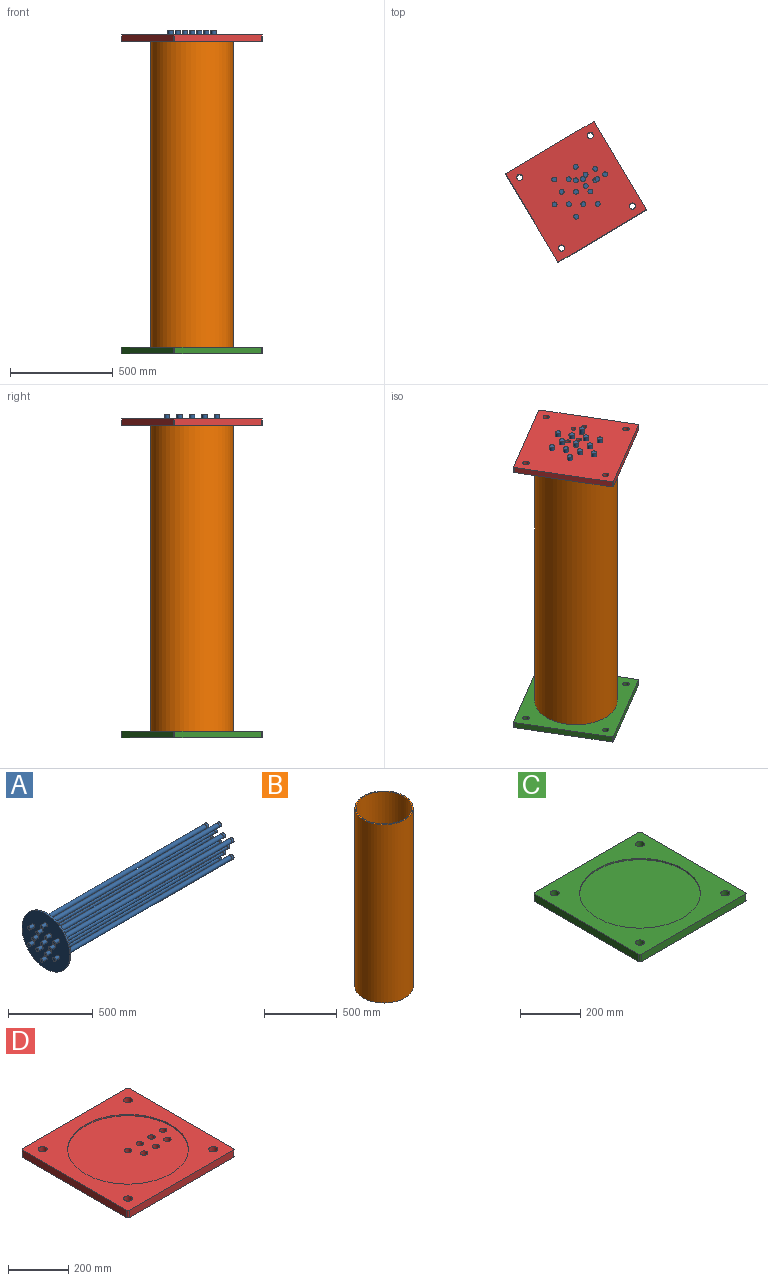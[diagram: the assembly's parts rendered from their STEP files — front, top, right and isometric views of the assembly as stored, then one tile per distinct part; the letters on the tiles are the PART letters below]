
ASSEMBLY  parts=4 mates=6
PART A: 133 faces, bbox 1490x400x400 mm
  f0: plane 31.5x31.5mm, normal (1,0,0), area 779.3mm2, adj f1
  f1: cylinder r=15.75mm len=31.5mm, axis (-1,0,0), area 1682.3mm2, adj f0,f2
  f2: plane 31.5x31.5mm, normal (-1,0,0), area 72.5mm2, adj f1,f3
  f3: cylinder r=15mm len=1394mm, axis (-1,0,0), area 131381.4mm2, adj f2,f4
  f4: plane 31.5x31.5mm, normal (1,0,0), area 72.5mm2, adj f3,f5
  f5: cylinder r=15.75mm len=31.5mm, axis (-1,0,0), area 2375mm2, adj f4,f6
  f6: plane 40x40mm, normal (1,0,0), area 477.3mm2, adj f5,f7
  f7: cylinder r=20mm len=40mm, axis (-1,0,0), area 1005.3mm2, adj f6,f106
  f8: plane 31.5x31.5mm, normal (1,0,0), area 779.3mm2, adj f9
  f9: cylinder r=15.75mm len=31.5mm, axis (-1,0,0), area 1682.3mm2, adj f8,f10
  f10: plane 31.5x31.5mm, normal (-1,0,0), area 72.5mm2, adj f9,f11
  f11: cylinder r=15mm len=1394mm, axis (-1,0,0), area 131381.4mm2, adj f10,f12
  f12: plane 31.5x31.5mm, normal (1,0,0), area 72.5mm2, adj f11,f13
  f13: cylinder r=15.75mm len=31.5mm, axis (-1,0,0), area 2375mm2, adj f12,f14
  f14: plane 40x40mm, normal (1,0,0), area 477.3mm2, adj f13,f15
  f15: cylinder r=20mm len=40mm, axis (-1,0,0), area 1005.3mm2, adj f14,f106
  f16: plane 31.5x31.5mm, normal (1,0,0), area 779.3mm2, adj f17
  f17: cylinder r=15.75mm len=31.5mm, axis (-1,0,0), area 1682.3mm2, adj f16,f18
  f18: plane 31.5x31.5mm, normal (-1,0,0), area 72.5mm2, adj f17,f19
  f19: cylinder r=15mm len=1394mm, axis (-1,0,0), area 131381.4mm2, adj f18,f20
  f20: plane 31.5x31.5mm, normal (1,0,0), area 72.5mm2, adj f19,f21
  f21: cylinder r=15.75mm len=31.5mm, axis (-1,0,0), area 2375mm2, adj f20,f22
  f22: plane 40x40mm, normal (1,0,0), area 477.3mm2, adj f21,f23
  f23: cylinder r=20mm len=40mm, axis (-1,0,0), area 1005.3mm2, adj f22,f106
  f24: plane 31.5x31.5mm, normal (1,0,0), area 779.3mm2, adj f25
  f25: cylinder r=15.75mm len=31.5mm, axis (-1,0,0), area 1682.3mm2, adj f24,f26
  f26: plane 31.5x31.5mm, normal (-1,0,0), area 72.5mm2, adj f25,f27
  f27: cylinder r=15mm len=1394mm, axis (-1,0,0), area 131381.4mm2, adj f26,f28
  f28: plane 31.5x31.5mm, normal (1,0,0), area 72.5mm2, adj f27,f29
  f29: cylinder r=15.75mm len=31.5mm, axis (-1,0,0), area 2375mm2, adj f28,f30
  f30: plane 40x40mm, normal (1,0,0), area 477.3mm2, adj f29,f31
  f31: cylinder r=20mm len=40mm, axis (-1,0,0), area 1005.3mm2, adj f30,f106
  f32: plane 31.5x31.5mm, normal (1,0,0), area 779.3mm2, adj f33
  f33: cylinder r=15.75mm len=31.5mm, axis (-1,0,0), area 1682.3mm2, adj f32,f34
  f34: plane 31.5x31.5mm, normal (-1,0,0), area 72.5mm2, adj f33,f35
  f35: cylinder r=15mm len=1394mm, axis (-1,0,0), area 131381.4mm2, adj f34,f36
  f36: plane 31.5x31.5mm, normal (1,0,0), area 72.5mm2, adj f35,f37
  f37: cylinder r=15.75mm len=31.5mm, axis (-1,0,0), area 2375mm2, adj f36,f38
  f38: plane 40x40mm, normal (1,0,0), area 477.3mm2, adj f37,f39
  f39: cylinder r=20mm len=40mm, axis (-1,0,0), area 1005.3mm2, adj f38,f106
  f40: plane 31.5x31.5mm, normal (1,0,0), area 779.3mm2, adj f41
  f41: cylinder r=15.75mm len=31.5mm, axis (-1,0,0), area 1682.3mm2, adj f40,f42
  f42: plane 31.5x31.5mm, normal (-1,0,0), area 72.5mm2, adj f41,f43
  f43: cylinder r=15mm len=1394mm, axis (-1,0,0), area 131381.4mm2, adj f42,f44
  f44: plane 31.5x31.5mm, normal (1,0,0), area 72.5mm2, adj f43,f45
  f45: cylinder r=15.75mm len=31.5mm, axis (-1,0,0), area 2375mm2, adj f44,f46
  f46: plane 40x40mm, normal (1,0,0), area 477.3mm2, adj f45,f47
  f47: cylinder r=20mm len=40mm, axis (-1,0,0), area 1005.3mm2, adj f46,f106
  f48: plane 31.5x31.5mm, normal (1,0,0), area 779.3mm2, adj f49
  f49: cylinder r=15.75mm len=31.5mm, axis (-1,0,0), area 1682.3mm2, adj f48,f50
  f50: plane 31.5x31.5mm, normal (-1,0,0), area 72.5mm2, adj f49,f51
  f51: cylinder r=15mm len=1394mm, axis (-1,0,0), area 131381.4mm2, adj f50,f52
  f52: plane 31.5x31.5mm, normal (1,0,0), area 72.5mm2, adj f51,f53
  f53: cylinder r=15.75mm len=31.5mm, axis (-1,0,0), area 2375mm2, adj f52,f54
  f54: plane 40x40mm, normal (1,0,0), area 477.3mm2, adj f53,f55
  f55: cylinder r=20mm len=40mm, axis (-1,0,0), area 1005.3mm2, adj f54,f106
  f56: plane 31.5x31.5mm, normal (1,0,0), area 779.3mm2, adj f57
  f57: cylinder r=15.75mm len=31.5mm, axis (-1,0,0), area 1682.3mm2, adj f56,f58
  f58: plane 31.5x31.5mm, normal (-1,0,0), area 72.5mm2, adj f57,f59
  f59: cylinder r=15mm len=1394mm, axis (-1,0,0), area 131381.4mm2, adj f58,f60
  f60: plane 31.5x31.5mm, normal (1,0,0), area 72.5mm2, adj f59,f61
  f61: cylinder r=15.75mm len=31.5mm, axis (-1,0,0), area 2375mm2, adj f60,f62
  f62: plane 40x40mm, normal (1,0,0), area 477.3mm2, adj f61,f63
  f63: cylinder r=20mm len=40mm, axis (-1,0,0), area 1005.3mm2, adj f62,f106
  f64: plane 31.5x31.5mm, normal (1,0,0), area 779.3mm2, adj f65
  f65: cylinder r=15.75mm len=31.5mm, axis (-1,0,0), area 1682.3mm2, adj f64,f66
  f66: plane 31.5x31.5mm, normal (-1,0,0), area 72.5mm2, adj f65,f67
  f67: cylinder r=15mm len=1394mm, axis (-1,0,0), area 131381.4mm2, adj f66,f68
  f68: plane 31.5x31.5mm, normal (1,0,0), area 72.5mm2, adj f67,f69
  f69: cylinder r=15.75mm len=31.5mm, axis (-1,0,0), area 2375mm2, adj f68,f70
  f70: plane 40x40mm, normal (1,0,0), area 477.3mm2, adj f69,f71
  f71: cylinder r=20mm len=40mm, axis (-1,0,0), area 1005.3mm2, adj f70,f106
  f72: plane 31.5x31.5mm, normal (1,0,0), area 779.3mm2, adj f73
  f73: cylinder r=15.75mm len=31.5mm, axis (-1,0,0), area 1682.3mm2, adj f72,f74
  f74: plane 31.5x31.5mm, normal (-1,0,0), area 72.5mm2, adj f73,f75
  f75: cylinder r=15mm len=1394mm, axis (-1,0,0), area 131381.4mm2, adj f74,f76
  f76: plane 31.5x31.5mm, normal (1,0,0), area 72.5mm2, adj f75,f77
  f77: cylinder r=15.75mm len=31.5mm, axis (-1,0,0), area 2375mm2, adj f76,f78
  f78: plane 40x40mm, normal (1,0,0), area 477.3mm2, adj f77,f79
  f79: cylinder r=20mm len=40mm, axis (-1,0,0), area 1005.3mm2, adj f78,f106
  f80: plane 31.5x31.5mm, normal (1,0,0), area 779.3mm2, adj f81
  f81: cylinder r=15.75mm len=31.5mm, axis (-1,0,0), area 1682.3mm2, adj f80,f82
  f82: plane 31.5x31.5mm, normal (-1,0,0), area 72.5mm2, adj f81,f83
  f83: cylinder r=15mm len=1394mm, axis (-1,0,0), area 131381.4mm2, adj f82,f84
  f84: plane 31.5x31.5mm, normal (1,0,0), area 72.5mm2, adj f83,f85
  f85: cylinder r=15.75mm len=31.5mm, axis (-1,0,0), area 2375mm2, adj f84,f86
  f86: plane 40x40mm, normal (1,0,0), area 477.3mm2, adj f85,f87
  f87: cylinder r=20mm len=40mm, axis (-1,0,0), area 1005.3mm2, adj f86,f106
  f88: plane 31.5x31.5mm, normal (1,0,0), area 779.3mm2, adj f89
  f89: cylinder r=15.75mm len=31.5mm, axis (-1,0,0), area 1682.3mm2, adj f88,f90
  f90: plane 31.5x31.5mm, normal (-1,0,0), area 72.5mm2, adj f89,f91
  f91: cylinder r=15mm len=1394mm, axis (-1,0,0), area 131381.4mm2, adj f90,f92
  f92: plane 31.5x31.5mm, normal (1,0,0), area 72.5mm2, adj f91,f93
  f93: cylinder r=15.75mm len=31.5mm, axis (-1,0,0), area 2375mm2, adj f92,f94
  f94: plane 40x40mm, normal (1,0,0), area 477.3mm2, adj f93,f95
  f95: cylinder r=20mm len=40mm, axis (-1,0,0), area 1005.3mm2, adj f94,f106
  f96: plane 31.5x31.5mm, normal (1,0,0), area 779.3mm2, adj f97
  f97: cylinder r=15.75mm len=31.5mm, axis (-1,0,0), area 1682.3mm2, adj f96,f98
  f98: plane 31.5x31.5mm, normal (-1,0,0), area 72.5mm2, adj f97,f99
  f99: cylinder r=15mm len=1394mm, axis (-1,0,0), area 131381.4mm2, adj f98,f100
  f100: plane 31.5x31.5mm, normal (1,0,0), area 72.5mm2, adj f99,f101
  f101: cylinder r=15.75mm len=31.5mm, axis (-1,0,0), area 2375mm2, adj f100,f102
  f102: plane 40x40mm, normal (1,0,0), area 477.3mm2, adj f101,f103
  f103: cylinder r=20mm len=40mm, axis (-1,0,0), area 1005.3mm2, adj f102,f106
  f104: cylinder r=200mm len=400mm, axis (1,0,0), area 12566.4mm2, adj f105,f106
  f105: plane 400x400mm, normal (-1,0,0), area 119880.3mm2, adj f104,f108,f110,f112,f114,f116,f118,f120
  f106: plane 400x400mm, normal (1,0,0), area 109327.4mm2, adj f7,f15,f23,f31,f39,f47,f55,f63
  f107: plane 23.8x23.8mm, normal (-1,0,0), area 444.9mm2, adj f108
  f108: cylinder r=11.9mm len=37mm, axis (-1,0,0), area 2766.5mm2, adj f105,f107
  f109: plane 23.8x23.8mm, normal (-1,0,0), area 444.9mm2, adj f110
  f110: cylinder r=11.9mm len=37mm, axis (-1,0,0), area 2766.5mm2, adj f105,f109
  f111: plane 23.8x23.8mm, normal (-1,0,0), area 444.9mm2, adj f112
  f112: cylinder r=11.9mm len=37mm, axis (-1,0,0), area 2766.5mm2, adj f105,f111
  f113: plane 23.8x23.8mm, normal (-1,0,0), area 444.9mm2, adj f114
  f114: cylinder r=11.9mm len=37mm, axis (-1,0,0), area 2766.5mm2, adj f105,f113
  f115: plane 23.8x23.8mm, normal (-1,0,0), area 444.9mm2, adj f116
  f116: cylinder r=11.9mm len=37mm, axis (-1,0,0), area 2766.5mm2, adj f105,f115
  f117: plane 23.8x23.8mm, normal (-1,0,0), area 444.9mm2, adj f118
  f118: cylinder r=11.9mm len=37mm, axis (-1,0,0), area 2766.5mm2, adj f105,f117
  f119: plane 23.8x23.8mm, normal (-1,0,0), area 444.9mm2, adj f120
  f120: cylinder r=11.9mm len=37mm, axis (-1,0,0), area 2766.5mm2, adj f105,f119
  f121: plane 23.8x23.8mm, normal (-1,0,0), area 444.9mm2, adj f122
  f122: cylinder r=11.9mm len=37mm, axis (-1,0,0), area 2766.5mm2, adj f105,f121
  f123: plane 23.8x23.8mm, normal (-1,0,0), area 444.9mm2, adj f124
  f124: cylinder r=11.9mm len=37mm, axis (-1,0,0), area 2766.5mm2, adj f105,f123
  f125: plane 23.8x23.8mm, normal (-1,0,0), area 444.9mm2, adj f126
  f126: cylinder r=11.9mm len=37mm, axis (-1,0,0), area 2766.5mm2, adj f105,f125
  f127: plane 23.8x23.8mm, normal (-1,0,0), area 444.9mm2, adj f128
  f128: cylinder r=11.9mm len=37mm, axis (-1,0,0), area 2766.5mm2, adj f105,f127
  f129: plane 23.8x23.8mm, normal (-1,0,0), area 444.9mm2, adj f130
  f130: cylinder r=11.9mm len=37mm, axis (-1,0,0), area 2766.5mm2, adj f105,f129
  f131: plane 23.8x23.8mm, normal (-1,0,0), area 444.9mm2, adj f132
  f132: cylinder r=11.9mm len=37mm, axis (-1,0,0), area 2766.5mm2, adj f105,f131
PART B: 4 faces, bbox 400x400x1500 mm
  f0: cylinder r=192mm len=1500mm, axis (0,0,-1), area 1809557.4mm2, adj f2,f3
  f1: cylinder r=200mm len=1500mm, axis (0,0,-1), area 1884955.6mm2, adj f2,f3
  f2: plane 400x400mm, normal (0,0,1), area 9852mm2, adj f0,f1
  f3: plane 400x400mm, normal (0,0,-1), area 9852mm2, adj f0,f1
PART C: 16 faces, bbox 500x500x30 mm
  f0: plane 490x30mm, normal (1,0,0), area 14700mm2, adj f8,f9,f10,f13
  f1: plane 490x30mm, normal (0,1,0), area 14700mm2, adj f8,f9,f10,f11
  f2: plane 490x30mm, normal (-1,0,0), area 14700mm2, adj f8,f9,f11,f12
  f3: cylinder r=15mm len=30mm, axis (0,0,-1), area 2827.4mm2, adj f8,f9
  f4: plane 490x30mm, normal (0,-1,0), area 14700mm2, adj f8,f9,f12,f13
  f5: cylinder r=15mm len=30mm, axis (0,0,-1), area 2827.4mm2, adj f8,f9
  f6: cylinder r=15mm len=30mm, axis (0,0,-1), area 2827.4mm2, adj f8,f9
  f7: cylinder r=15mm len=30mm, axis (0,0,-1), area 2827.4mm2, adj f8,f9
  f8: plane 500x500mm, normal (0,0,1), area 121487.4mm2, adj f0,f1,f2,f3,f4,f5,f6,f7
  f9: plane 500x500mm, normal (0,0,-1), area 247151.1mm2, adj f0,f1,f2,f3,f4,f5,f6,f7
  f10: cylinder r=5mm len=30mm, axis (0,0,-1), area 235.6mm2, adj f0,f1,f8,f9
  f11: cylinder r=5mm len=30mm, axis (0,0,1), area 235.6mm2, adj f1,f2,f8,f9
  f12: cylinder r=5mm len=30mm, axis (0,0,-1), area 235.6mm2, adj f2,f4,f8,f9
  f13: cylinder r=5mm len=30mm, axis (0,0,1), area 235.6mm2, adj f0,f4,f8,f9
  f14: cylinder r=200mm len=400mm, axis (0,0,1), area 6283.2mm2, adj f8,f15
  f15: plane 400x400mm, normal (0,0,1), area 125663.7mm2, adj f14
PART D: 23 faces, bbox 500x500x30 mm
  f0: cylinder r=12.05mm len=25mm, axis (0,0,-1), area 1892.8mm2, adj f16,f22
  f1: cylinder r=12.05mm len=25mm, axis (0,0,-1), area 1892.8mm2, adj f16,f22
  f2: cylinder r=12.05mm len=25mm, axis (0,0,-1), area 1892.8mm2, adj f16,f22
  f3: cylinder r=12.05mm len=25mm, axis (0,0,-1), area 1892.8mm2, adj f16,f22
  f4: cylinder r=12.05mm len=25mm, axis (0,0,-1), area 1892.8mm2, adj f16,f22
  f5: cylinder r=12.05mm len=25mm, axis (0,0,-1), area 1892.8mm2, adj f16,f22
  f6: cylinder r=12.05mm len=25mm, axis (0,0,-1), area 1892.8mm2, adj f16,f22
  f7: plane 490x30mm, normal (1,0,0), area 14700mm2, adj f15,f16,f17,f20
  f8: plane 490x30mm, normal (0,1,0), area 14700mm2, adj f15,f16,f17,f18
  f9: plane 490x30mm, normal (-1,0,0), area 14700mm2, adj f15,f16,f18,f19
  f10: cylinder r=15mm len=30mm, axis (0,0,-1), area 2827.4mm2, adj f15,f16
  f11: plane 490x30mm, normal (0,-1,0), area 14700mm2, adj f15,f16,f19,f20
  f12: cylinder r=15mm len=30mm, axis (0,0,-1), area 2827.4mm2, adj f15,f16
  f13: cylinder r=15mm len=30mm, axis (0,0,-1), area 2827.4mm2, adj f15,f16
  f14: cylinder r=15mm len=30mm, axis (0,0,-1), area 2827.4mm2, adj f15,f16
  f15: plane 500x500mm, normal (0,0,1), area 121487.4mm2, adj f7,f8,f9,f10,f11,f12,f13,f14
  f16: plane 500x500mm, normal (0,0,-1), area 243957.9mm2, adj f0,f1,f2,f3,f4,f5,f6,f7
  f17: cylinder r=5mm len=30mm, axis (0,0,-1), area 235.6mm2, adj f7,f8,f15,f16
  f18: cylinder r=5mm len=30mm, axis (0,0,1), area 235.6mm2, adj f8,f9,f15,f16
  f19: cylinder r=5mm len=30mm, axis (0,0,-1), area 235.6mm2, adj f9,f11,f15,f16
  f20: cylinder r=5mm len=30mm, axis (0,0,1), area 235.6mm2, adj f7,f11,f15,f16
  f21: cylinder r=200mm len=400mm, axis (0,0,1), area 6283.2mm2, adj f15,f22
  f22: plane 400x400mm, normal (0,0,1), area 122470.5mm2, adj f0,f1,f2,f3,f4,f5,f6,f21
PLACE A rot(axis=(-0.26,0.93,0.26),94deg) t=(0,0,1547)mm
PLACE B at identity
PLACE C rot(axis=(0,0,-1),59.3deg) t=(0,0,-25)mm
PLACE D rot(axis=(-0.96,-0.26,0),180deg) t=(0,0,1525)mm
MATE cylindrical D.f21 <-> B.f0  axis (0,0,-1) through (0,0,1495)mm
MATE planar D.f22 <-> A.f1  axis (0,0,-1) through (-1.58,-1.56,1500)mm
MATE cylindrical A.f1 <-> D.f0  axis (0,0,1) through (0,0,1547)mm
MATE revolute C.f14 <-> B.f0  axis (0,0,1) through (0,0,0)mm
MATE parallel D.f9 <-> C.f4  axis (-0.86,-0.51,0) through (-214.94,-127.67,1510)mm
MATE planar D.f22 <-> B.f0  axis (0,0,-1) through (-1.58,-1.56,1500)mm
